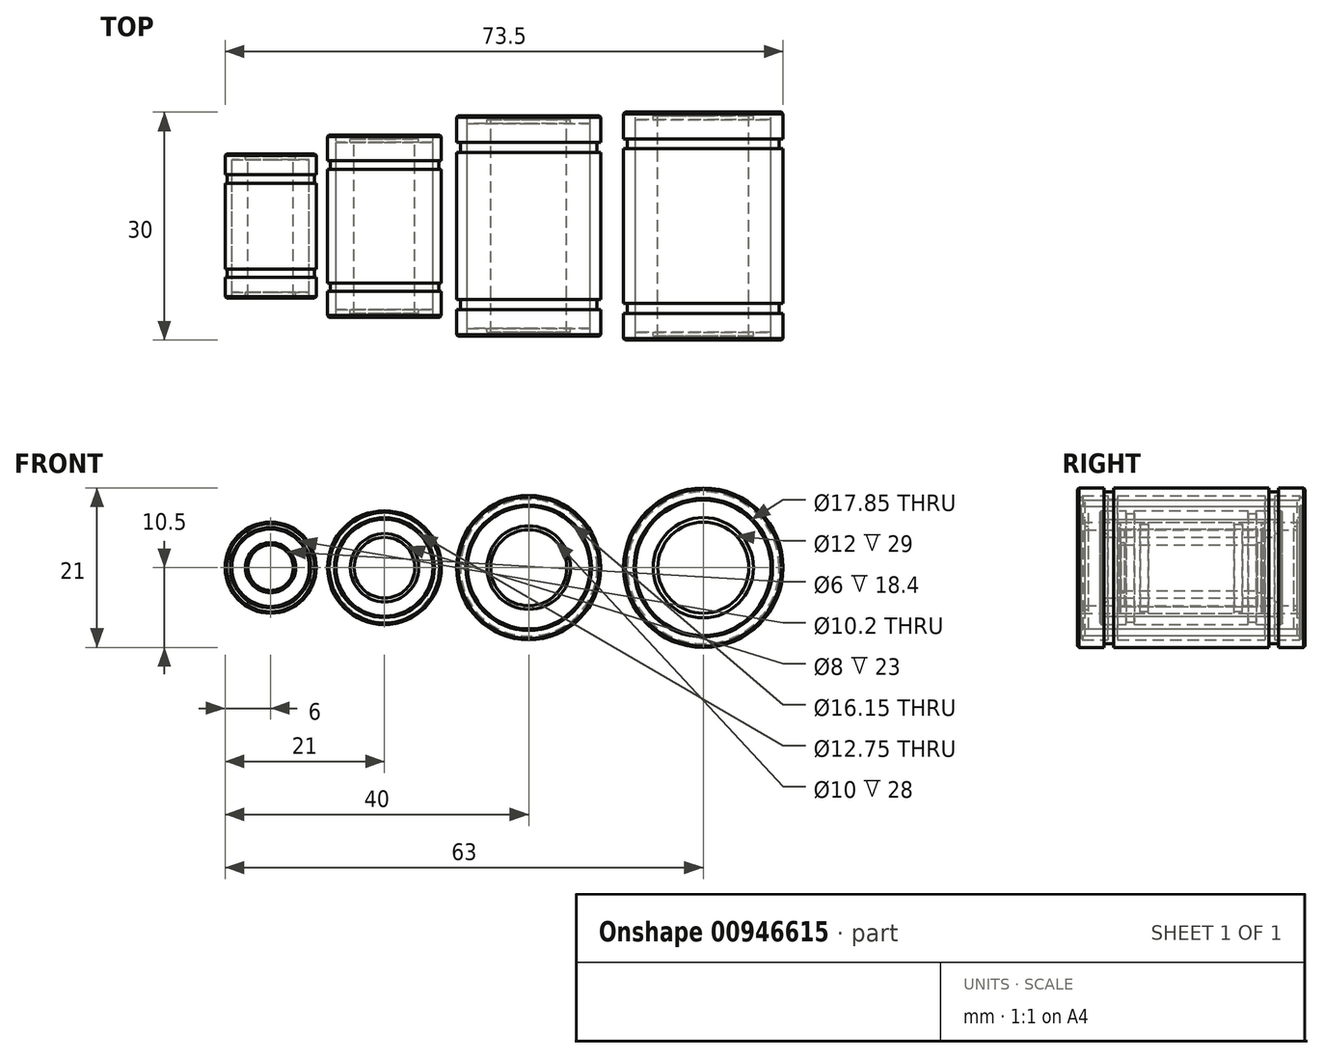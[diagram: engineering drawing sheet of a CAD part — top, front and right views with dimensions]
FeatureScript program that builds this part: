
annotation { "Feature Type Name" : "Feature", "Feature Type Description" : "" }
export const myFeature = defineFeature(function(context is Context, id is Id, definition is map)
    precondition{}
    {
        {
            var Q0;
            Q0=qCreatedBy(makeId("Front.planeOp"),FACE);
            var sketch = newSketch(context, id + "F0", { "sketchPlane" : qUnion([Q0])});
            skCircle(sketch, "E0", {"center": v(0, 0) * mm, "radius": 7.5 * mm});
            skCircle(sketch, "E1", {"center": v(0, 0) * mm, "radius": 6.38 * mm});
            skCircle(sketch, "E2", {"center": v(0, 0) * mm, "radius": 4 * mm});
            skCircle(sketch, "E3", {"center": v(0, 0) * mm, "radius": 4.5 * mm});
            skCircle(sketch, "E4", {"center": v(-15, 0) * mm, "radius": 6 * mm});
            skCircle(sketch, "E5", {"center": v(-15, 0) * mm, "radius": 5.1 * mm});
            skCircle(sketch, "E6", {"center": v(-15, 0) * mm, "radius": 3 * mm});
            skCircle(sketch, "E7", {"center": v(-15, 0) * mm, "radius": 3.3 * mm});
            skLineSegment(sketch, "E8", {"start": v(-27.58, 0) * mm, "end": v(56.16, 0) * mm, "construction": true});
            skCircle(sketch, "E9", {"center": v(19, 0) * mm, "radius": 9.5 * mm});
            skCircle(sketch, "E10", {"center": v(19, 0) * mm, "radius": 8.07 * mm});
            skCircle(sketch, "E11", {"center": v(19, 0) * mm, "radius": 5 * mm});
            skCircle(sketch, "E12", {"center": v(19, 0) * mm, "radius": 5.5 * mm});
            skCircle(sketch, "E13", {"center": v(42, 0) * mm, "radius": 10.5 * mm});
            skCircle(sketch, "E14", {"center": v(42, 0) * mm, "radius": 8.92 * mm});
            skCircle(sketch, "E15", {"center": v(42, 0) * mm, "radius": 6 * mm});
            skCircle(sketch, "E16", {"center": v(42, 0) * mm, "radius": 6.6 * mm});
            skSolve(sketch);
        }
        {
            var Q0;
            Q0=makeQuery(id+"F0.imprint","IMPRINT",FACE,{"disambiguationData":[TD([[makeQuery(id+"F0.imprint","IMPRINT",EDGE,{"derivedFrom":sQuery(id+"F0.wireOp",EDGE,"E4")}),1.0]])]});
            extrude(context, id + "F1", {"entities" : qUnion([Q0]), "depth" : 19 * mm, "offsetDistance" : 25 * mm, "symmetric" : true});
        }
        {
            var Q0;
            Q0=makeQuery(id+"F0.imprint","IMPRINT",FACE,{"disambiguationData":[TD([[makeQuery(id+"F0.imprint","IMPRINT",EDGE,{"derivedFrom":sQuery(id+"F0.wireOp",EDGE,"E5")}),1.0]])]});
            extrude(context, id + "F2", {"entities" : qUnion([Q0]), "depth" : 17.5 * mm, "offsetDistance" : 25 * mm, "symmetric" : true});
        }
        {
            var Q0;
            Q0=makeQuery(id+"F0.imprint","IMPRINT",FACE,{"disambiguationData":[TD([[makeQuery(id+"F0.imprint","IMPRINT",EDGE,{"derivedFrom":sQuery(id+"F0.wireOp",EDGE,"E6")}),-1.0]])]});
            extrude(context, id + "F3", {"entities" : qUnion([Q0]), "operationType" : NewBodyOperationType.ADD, "depth" : 18.4 * mm, "offsetDistance" : 25 * mm, "symmetric" : true});
        }
        {
            var Q0;
            Q0=qCreatedBy(makeId("Right.planeOp"),FACE);
            var Q1;
            Q1=sQuery(id+"F0.wireOp",VERTEX,"E4.center");
            cPlane(context, id + "F4", {"entities" : qUnion([Q0, Q1]), "cplaneType" : CPlaneType.PLANE_POINT, "offset" : 25 * mm, "width" : 150 * mm, "height" : 150 * mm});
        }
        {
            var Q0;
            Q0=qCreatedBy(id+"F4.planeOp",FACE);
            var sketch = newSketch(context, id + "F5", { "sketchPlane" : qUnion([Q0])});
            skLineSegment(sketch, "E17", {"start": v(-12, 0) * mm, "end": v(12, 0) * mm, "construction": true});
            skLineSegment(sketch, "E18", {"start": v(0, 0) * mm, "end": v(0, 7.16) * mm, "construction": true});
            skLineSegment(sketch, "E19.bottom", {"start": v(-6.75, 6.75) * mm, "end": v(-5.65, 6.75) * mm});
            skLineSegment(sketch, "E19.top", {"start": v(-6.75, 5.75) * mm, "end": v(-5.65, 5.75) * mm});
            skLineSegment(sketch, "E19.left", {"start": v(-6.75, 6.75) * mm, "end": v(-6.75, 5.75) * mm});
            skLineSegment(sketch, "E19.right", {"start": v(-5.65, 6.75) * mm, "end": v(-5.65, 5.75) * mm});
            skLineSegment(sketch, "E20.MirrorCS", {"start": v(5.65, 6.75) * mm, "end": v(5.65, 5.75) * mm});
            skLineSegment(sketch, "E21.MirrorCS", {"start": v(6.75, 6.75) * mm, "end": v(6.75, 5.75) * mm});
            skLineSegment(sketch, "E22.MirrorCS", {"start": v(6.75, 5.75) * mm, "end": v(5.65, 5.75) * mm});
            skLineSegment(sketch, "E23.MirrorCS", {"start": v(6.75, 6.75) * mm, "end": v(5.65, 6.75) * mm});
            skSolve(sketch);
        }
        {
            var Q0;
            Q0=makeQuery(id+"F5.imprint","IMPRINT",FACE,{"disambiguationData":[TD([[makeQuery(id+"F5.imprint","IMPRINT",EDGE,{"derivedFrom":sQuery(id+"F5.wireOp",EDGE,"E20.MirrorCS")}),1.0]])]});
            var Q1;
            Q1=makeQuery(id+"F5.imprint","IMPRINT",FACE,{"disambiguationData":[TD([[makeQuery(id+"F5.imprint","IMPRINT",EDGE,{"derivedFrom":sQuery(id+"F5.wireOp",EDGE,"E19.bottom")}),-1.0]])]});
            var Q2;
            Q2=sQuery(id+"F5.wireOp",EDGE,"E17");
            revolve(context, id + "F6", {"operationType" : NewBodyOperationType.REMOVE, "surfaceOperationType" : NewSurfaceOperationType.NEW, "entities" : qUnion([Q0, Q1]), "axis" : qUnion([Q2]), "revolveType" : RevolveType.FULL, "oppositeDirection" : true});
        }
        {
            var Q0;
            Q0=makeQuery(id+"F1.opExtrude","CAP_FACE",FACE,{"disambiguationData":[OSD([sQuery(id+"F0.wireOp",EDGE,"E4"),sQuery(id+"F0.wireOp",EDGE,"E5")])],"isStart":false});
            var Q1;
            Q1=makeQuery(id+"F1.opExtrude","CAP_FACE",FACE,{"disambiguationData":[OSD([sQuery(id+"F0.wireOp",EDGE,"E4"),sQuery(id+"F0.wireOp",EDGE,"E5")])],"isStart":true});
            chamfer(context, id + "F7", {"entities" : qUnion([Q0, Q1]), "width" : 0.2 * mm, "tangentPropagation" : true});
        }
        {
            var Q0;
            Q0=makeQuery(id+"F0.imprint","IMPRINT",FACE,{"disambiguationData":[TD([[makeQuery(id+"F0.imprint","IMPRINT",EDGE,{"derivedFrom":sQuery(id+"F0.wireOp",EDGE,"E0")}),1.0]])]});
            extrude(context, id + "F8", {"entities" : qUnion([Q0]), "depth" : 24 * mm, "symmetric" : true});
        }
        {
            var Q0;
            Q0=makeQuery(id+"F0.imprint","IMPRINT",FACE,{"disambiguationData":[TD([[makeQuery(id+"F0.imprint","IMPRINT",EDGE,{"derivedFrom":sQuery(id+"F0.wireOp",EDGE,"E1")}),1.0]])]});
            extrude(context, id + "F9", {"entities" : qUnion([Q0]), "depth" : 22 * mm, "symmetric" : true});
        }
        {
            var Q0;
            Q0=makeQuery(id+"F0.imprint","IMPRINT",FACE,{"disambiguationData":[TD([[makeQuery(id+"F0.imprint","IMPRINT",EDGE,{"derivedFrom":sQuery(id+"F0.wireOp",EDGE,"E2")}),-1.0]])]});
            extrude(context, id + "F10", {"entities" : qUnion([Q0]), "operationType" : NewBodyOperationType.ADD, "depth" : 23 * mm, "symmetric" : true});
        }
        {
            var Q0;
            Q0=qCreatedBy(makeId("Right.planeOp"),FACE);
            var sketch = newSketch(context, id + "F11", { "sketchPlane" : qUnion([Q0])});
            skLineSegment(sketch, "E24", {"start": v(-12, 0) * mm, "end": v(12, 0) * mm, "construction": true});
            skLineSegment(sketch, "E25", {"start": v(0, 0) * mm, "end": v(0, 7.48) * mm, "construction": true});
            skLineSegment(sketch, "E26.bottom", {"start": v(-8.6, 8) * mm, "end": v(-7.5, 8) * mm});
            skLineSegment(sketch, "E26.top", {"start": v(-8.6, 7.15) * mm, "end": v(-7.5, 7.15) * mm});
            skLineSegment(sketch, "E26.left", {"start": v(-8.6, 8) * mm, "end": v(-8.6, 7.15) * mm});
            skLineSegment(sketch, "E26.right", {"start": v(-7.5, 8) * mm, "end": v(-7.5, 7.15) * mm});
            skLineSegment(sketch, "E27.MirrorCS", {"start": v(7.5, 8) * mm, "end": v(7.5, 7.15) * mm});
            skLineSegment(sketch, "E28.MirrorCS", {"start": v(8.6, 8) * mm, "end": v(8.6, 7.15) * mm});
            skLineSegment(sketch, "E29.MirrorCS", {"start": v(8.6, 7.15) * mm, "end": v(7.5, 7.15) * mm});
            skLineSegment(sketch, "E30.MirrorCS", {"start": v(8.6, 8) * mm, "end": v(7.5, 8) * mm});
            skSolve(sketch);
        }
        {
            var Q0;
            Q0=makeQuery(id+"F11.imprint","IMPRINT",FACE,{"disambiguationData":[TD([[makeQuery(id+"F11.imprint","IMPRINT",EDGE,{"derivedFrom":sQuery(id+"F11.wireOp",EDGE,"E26.bottom")}),-1.0]])]});
            var Q1;
            Q1=makeQuery(id+"F11.imprint","IMPRINT",FACE,{"disambiguationData":[TD([[makeQuery(id+"F11.imprint","IMPRINT",EDGE,{"derivedFrom":sQuery(id+"F11.wireOp",EDGE,"E27.MirrorCS")}),1.0]])]});
            var Q2;
            Q2=sQuery(id+"F11.wireOp",EDGE,"E24");
            revolve(context, id + "F12", {"operationType" : NewBodyOperationType.REMOVE, "entities" : qUnion([Q0, Q1]), "axis" : qUnion([Q2]), "revolveType" : RevolveType.FULL, "oppositeDirection" : true});
        }
        {
            var Q0;
            Q0=makeQuery(id+"F8.opExtrude","CAP_FACE",FACE,{"disambiguationData":[OSD([sQuery(id+"F0.wireOp",EDGE,"E0"),sQuery(id+"F0.wireOp",EDGE,"E1")])],"isStart":false});
            var Q1;
            Q1=makeQuery(id+"F8.opExtrude","CAP_FACE",FACE,{"disambiguationData":[OSD([sQuery(id+"F0.wireOp",EDGE,"E0"),sQuery(id+"F0.wireOp",EDGE,"E1")])],"isStart":true});
            chamfer(context, id + "F13", {"entities" : qUnion([Q0, Q1]), "width" : .2 * mm, "tangentPropagation" : true});
        }
        {
            var Q0;
            Q0=makeQuery(id+"F0.imprint","IMPRINT",FACE,{"disambiguationData":[TD([[makeQuery(id+"F0.imprint","IMPRINT",EDGE,{"derivedFrom":sQuery(id+"F0.wireOp",EDGE,"E9")}),1.0]])]});
            extrude(context, id + "F14", {"entities" : qUnion([Q0]), "depth" : 29 * mm, "offsetDistance" : 25 * mm, "symmetric" : true});
        }
        {
            var Q0;
            Q0=makeQuery(id+"F0.imprint","IMPRINT",FACE,{"disambiguationData":[TD([[makeQuery(id+"F0.imprint","IMPRINT",EDGE,{"derivedFrom":sQuery(id+"F0.wireOp",EDGE,"E10")}),1.0]])]});
            extrude(context, id + "F15", {"entities" : qUnion([Q0]), "depth" : 27 * mm, "offsetDistance" : 25 * mm, "symmetric" : true});
        }
        {
            var Q0;
            Q0=makeQuery(id+"F0.imprint","IMPRINT",FACE,{"disambiguationData":[TD([[makeQuery(id+"F0.imprint","IMPRINT",EDGE,{"derivedFrom":sQuery(id+"F0.wireOp",EDGE,"E11")}),-1.0]])]});
            extrude(context, id + "F16", {"entities" : qUnion([Q0]), "operationType" : NewBodyOperationType.ADD, "depth" : 28 * mm, "offsetDistance" : 25 * mm, "symmetric" : true});
        }
        {
            var Q0;
            Q0=qCreatedBy(makeId("Right.planeOp"),FACE);
            var Q1;
            Q1=sQuery(id+"F0.wireOp",VERTEX,"E9.center");
            cPlane(context, id + "F17", {"entities" : qUnion([Q0, Q1]), "cplaneType" : CPlaneType.PLANE_POINT, "offset" : 25 * mm, "width" : 150 * mm, "height" : 150 * mm});
        }
        {
            var Q0;
            Q0=qCreatedBy(id+"F17.planeOp",FACE);
            var sketch = newSketch(context, id + "F18", { "sketchPlane" : qUnion([Q0])});
            skLineSegment(sketch, "E31", {"start": v(17.1, 0) * mm, "end": v(-21.39, 0) * mm, "construction": true});
            skLineSegment(sketch, "E32.bottom", {"start": v(11, 10) * mm, "end": v(9.7, 10) * mm});
            skLineSegment(sketch, "E32.top", {"start": v(11, 9) * mm, "end": v(9.7, 9) * mm});
            skLineSegment(sketch, "E32.left", {"start": v(11, 10) * mm, "end": v(11, 9) * mm});
            skLineSegment(sketch, "E32.right", {"start": v(9.7, 10) * mm, "end": v(9.7, 9) * mm});
            skLineSegment(sketch, "E33.bottom", {"start": v(-9.7, 10) * mm, "end": v(-11, 10) * mm});
            skLineSegment(sketch, "E33.top", {"start": v(-9.7, 9) * mm, "end": v(-11, 9) * mm});
            skLineSegment(sketch, "E33.left", {"start": v(-9.7, 10) * mm, "end": v(-9.7, 9) * mm});
            skLineSegment(sketch, "E33.right", {"start": v(-11, 10) * mm, "end": v(-11, 9) * mm});
            skLineSegment(sketch, "E34", {"start": v(0, 0) * mm, "end": v(0, 12.39) * mm, "construction": true});
            skSolve(sketch);
        }
        {
            var Q0;
            Q0=makeQuery(id+"F18.imprint","IMPRINT",FACE,{"disambiguationData":[TD([[makeQuery(id+"F18.imprint","IMPRINT",EDGE,{"derivedFrom":sQuery(id+"F18.wireOp",EDGE,"E32.bottom")}),1.0]])]});
            var Q1;
            Q1=makeQuery(id+"F18.imprint","IMPRINT",FACE,{"disambiguationData":[TD([[makeQuery(id+"F18.imprint","IMPRINT",EDGE,{"derivedFrom":sQuery(id+"F18.wireOp",EDGE,"E33.bottom")}),1.0]])]});
            var Q2;
            Q2=sQuery(id+"F18.wireOp",EDGE,"E31");
            revolve(context, id + "F19", {"operationType" : NewBodyOperationType.REMOVE, "surfaceOperationType" : NewSurfaceOperationType.NEW, "entities" : qUnion([Q0, Q1]), "axis" : qUnion([Q2]), "revolveType" : RevolveType.FULL, "oppositeDirection" : true});
        }
        {
            var Q0;
            Q0=makeQuery(id+"F14.opExtrude","CAP_FACE",FACE,{"disambiguationData":[OSD([sQuery(id+"F0.wireOp",EDGE,"E9"),sQuery(id+"F0.wireOp",EDGE,"E10")])],"isStart":false});
            var Q1;
            Q1=makeQuery(id+"F14.opExtrude","CAP_FACE",FACE,{"disambiguationData":[OSD([sQuery(id+"F0.wireOp",EDGE,"E9"),sQuery(id+"F0.wireOp",EDGE,"E10")])],"isStart":true});
            chamfer(context, id + "F20", {"entities" : qUnion([Q0, Q1]), "width" : 0.2 * mm, "tangentPropagation" : true});
        }
        {
            var Q0;
            Q0=makeQuery(id+"F0.imprint","IMPRINT",FACE,{"disambiguationData":[TD([[makeQuery(id+"F0.imprint","IMPRINT",EDGE,{"derivedFrom":sQuery(id+"F0.wireOp",EDGE,"E13")}),1.0]])]});
            extrude(context, id + "F21", {"entities" : qUnion([Q0]), "depth" : 30 * mm, "offsetDistance" : 25 * mm, "symmetric" : true});
        }
        {
            var Q0;
            Q0=makeQuery(id+"F0.imprint","IMPRINT",FACE,{"disambiguationData":[TD([[makeQuery(id+"F0.imprint","IMPRINT",EDGE,{"derivedFrom":sQuery(id+"F0.wireOp",EDGE,"E14")}),1.0]])]});
            extrude(context, id + "F22", {"entities" : qUnion([Q0]), "depth" : 28 * mm, "offsetDistance" : 25 * mm, "symmetric" : true});
        }
        {
            var Q0;
            Q0=makeQuery(id+"F0.imprint","IMPRINT",FACE,{"disambiguationData":[TD([[makeQuery(id+"F0.imprint","IMPRINT",EDGE,{"derivedFrom":sQuery(id+"F0.wireOp",EDGE,"E15")}),-1.0]])]});
            extrude(context, id + "F23", {"entities" : qUnion([Q0]), "operationType" : NewBodyOperationType.ADD, "depth" : 29 * mm, "offsetDistance" : 25 * mm, "symmetric" : true});
        }
        {
            var Q0;
            Q0=qCreatedBy(makeId("Right.planeOp"),FACE);
            var Q1;
            Q1=sQuery(id+"F0.wireOp",VERTEX,"E13.center");
            cPlane(context, id + "F24", {"entities" : qUnion([Q0, Q1]), "cplaneType" : CPlaneType.PLANE_POINT, "offset" : 25 * mm, "width" : 150 * mm, "height" : 150 * mm});
        }
        {
            var Q0;
            Q0=qCreatedBy(id+"F24.planeOp",FACE);
            var sketch = newSketch(context, id + "F25", { "sketchPlane" : qUnion([Q0])});
            skLineSegment(sketch, "E35", {"start": v(-11.48, 0) * mm, "end": v(12.25, 0) * mm, "construction": true});
            skLineSegment(sketch, "E36.bottom", {"start": v(-11.5, 11) * mm, "end": v(-10.2, 11) * mm});
            skLineSegment(sketch, "E36.top", {"start": v(-11.5, 10) * mm, "end": v(-10.2, 10) * mm});
            skLineSegment(sketch, "E36.left", {"start": v(-11.5, 11) * mm, "end": v(-11.5, 10) * mm});
            skLineSegment(sketch, "E36.right", {"start": v(-10.2, 11) * mm, "end": v(-10.2, 10) * mm});
            skLineSegment(sketch, "E37.bottom", {"start": v(10.2, 11) * mm, "end": v(11.5, 11) * mm});
            skLineSegment(sketch, "E37.top", {"start": v(10.2, 10) * mm, "end": v(11.5, 10) * mm});
            skLineSegment(sketch, "E37.left", {"start": v(10.2, 11) * mm, "end": v(10.2, 10) * mm});
            skLineSegment(sketch, "E37.right", {"start": v(11.5, 11) * mm, "end": v(11.5, 10) * mm});
            skLineSegment(sketch, "E38", {"start": v(0, 0) * mm, "end": v(0, 6.4) * mm, "construction": true});
            skSolve(sketch);
        }
        {
            var Q0;
            Q0=makeQuery(id+"F25.imprint","IMPRINT",FACE,{"disambiguationData":[TD([[makeQuery(id+"F25.imprint","IMPRINT",EDGE,{"derivedFrom":sQuery(id+"F25.wireOp",EDGE,"E36.bottom")}),-1.0]])]});
            var Q1;
            Q1=makeQuery(id+"F25.imprint","IMPRINT",FACE,{"disambiguationData":[TD([[makeQuery(id+"F25.imprint","IMPRINT",EDGE,{"derivedFrom":sQuery(id+"F25.wireOp",EDGE,"E37.bottom")}),-1.0]])]});
            var Q2;
            Q2=sQuery(id+"F25.wireOp",EDGE,"E35");
            revolve(context, id + "F26", {"operationType" : NewBodyOperationType.REMOVE, "surfaceOperationType" : NewSurfaceOperationType.NEW, "entities" : qUnion([Q0, Q1]), "axis" : qUnion([Q2]), "revolveType" : RevolveType.FULL, "oppositeDirection" : true});
        }
        {
            var Q0;
            Q0=makeQuery(id+"F21.opExtrude","CAP_FACE",FACE,{"disambiguationData":[OSD([sQuery(id+"F0.wireOp",EDGE,"E13"),sQuery(id+"F0.wireOp",EDGE,"E14")])],"isStart":true});
            var Q1;
            Q1=makeQuery(id+"F21.opExtrude","CAP_FACE",FACE,{"disambiguationData":[OSD([sQuery(id+"F0.wireOp",EDGE,"E13"),sQuery(id+"F0.wireOp",EDGE,"E14")])],"isStart":false});
            chamfer(context, id + "F27", {"entities" : qUnion([Q0, Q1]), "width" : 0.2 * mm, "tangentPropagation" : true});
        }
    });
